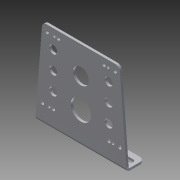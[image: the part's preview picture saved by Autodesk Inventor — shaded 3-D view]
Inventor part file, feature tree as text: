
AUTODESK INVENTOR PART (.ipt)
format: ipt  version: 2013 (Build 170138000, 138)  size: 118,784 bytes
history: native  units: in
note: dims shown in document units (in); Inventor stores cm internally (conversion verified against a paired STEP export)
features: other x2, plane x1, imported_body x1
ambient origin geometry x8: Origin, YZ Plane, XZ Plane, XY Plane, X Axis, Y Axis, Z Axis, Center Point
feature tree (4):
  other  "Toughbox-mini_d02"
  other  "Toughbox-mini_d021"
  plane  "Work Plane1"
  imported_body  "Base1"
